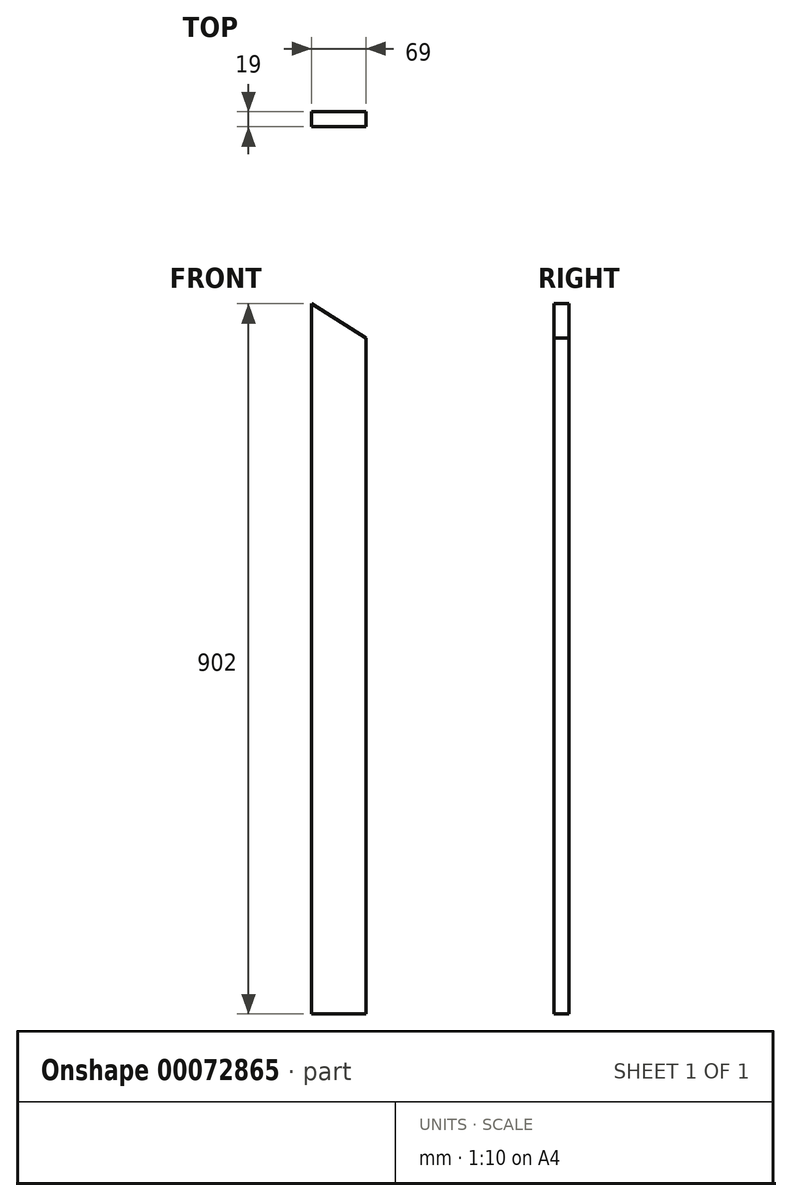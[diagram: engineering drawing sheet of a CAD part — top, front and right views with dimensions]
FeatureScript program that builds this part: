
annotation { "Feature Type Name" : "Feature", "Feature Type Description" : "" }
export const myFeature = defineFeature(function(context is Context, id is Id, definition is map)
    precondition{}
    {
        {
            var Q0;
            Q0=qCreatedBy(makeId("Front.planeOp"),FACE);
            var sketch = newSketch(context, id + "F0", { "sketchPlane" : qUnion([Q0])});
            skLineSegment(sketch, "E0", {"start": v(0, 0) * mm, "end": v(0, -902) * mm});
            skLineSegment(sketch, "E1", {"start": v(0, -902) * mm, "end": v(69, -902) * mm});
            skLineSegment(sketch, "E2", {"start": v(69, -902) * mm, "end": v(69, -43.62) * mm});
            skLineSegment(sketch, "E3", {"start": v(69, -43.62) * mm, "end": v(0, 0) * mm});
            skSolve(sketch);
        }
        {
            var Q0;
            Q0=makeQuery(id+"F0.imprint","IMPRINT",FACE,{"disambiguationData":[TD([[makeQuery(id+"F0.imprint","IMPRINT",EDGE,{"derivedFrom":sQuery(id+"F0.wireOp",EDGE,"E0")}),1.0]])]});
            extrude(context, id + "F1", {"entities" : qUnion([Q0]), "depth" : 19 * mm});
        }
    });
